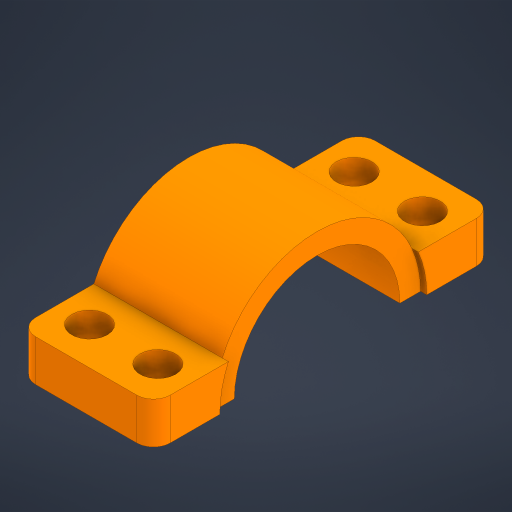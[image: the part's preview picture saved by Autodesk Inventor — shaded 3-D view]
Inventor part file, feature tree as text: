
AUTODESK INVENTOR PART (.ipt)
format: ipt  version: 2024 (Build 280153000, 153)  size: 247,296 bytes
history: native  units: mm
features: other x12, reference x7, sketch x3, extrude x3, fillet x1, mirror x1
ambient origin geometry x8: Origin, YZ Plane, XZ Plane, XY Plane, X Axis, Y Axis, Z Axis, Center Point
bodies: Body1 (feature_tree)
feature tree (27):
  other  "Твердое тело1"
  sketch  "Эскиз1"
  other  "РабПлоскость1"
  extrude  "Выдавливание1"  Depth=10.0mm TaperAngle=0.0deg
  fillet  "Сопряжение1"  Radius=2.0mm
  extrude  "Выдавливание2"  Depth=10.0mm TaperAngle=0.0deg
  other  "РабПлоскость2"
  sketch  "Эскиз3"
  other  "РабПлоскость3"
  extrude  "Выдавливание3"  Depth=10.0mm TaperAngle=0.0deg
  other  "РабПлоскость6"
  mirror  "Зеркальное отражение1"
  reference  "Ссылка1"
  reference  "Ссылка3"
  reference  "Ссылка4"
  sketch  "Эскиз2"
  reference  "Ссылка5"
  reference  "Ссылка6"
  reference  "Ссылка7"
  reference  "Ссылка8"
  parser-record x1  (decoder bookkeeping rows leaked as tree rows — omitted from the tree; the rows remain in map.json)
  other  "default_motor_asembly.iam"
  other  "lower_arm:1"
  other  "bushing_assembly:1"
  other  "bushing:1"
  other  "DIN 125-1 A A 4,3:4"
  other  "DIN 125-1 A A 4,3:3"
note: 1 file-system path scrubbed to <path> (originals preserved in map.json)
